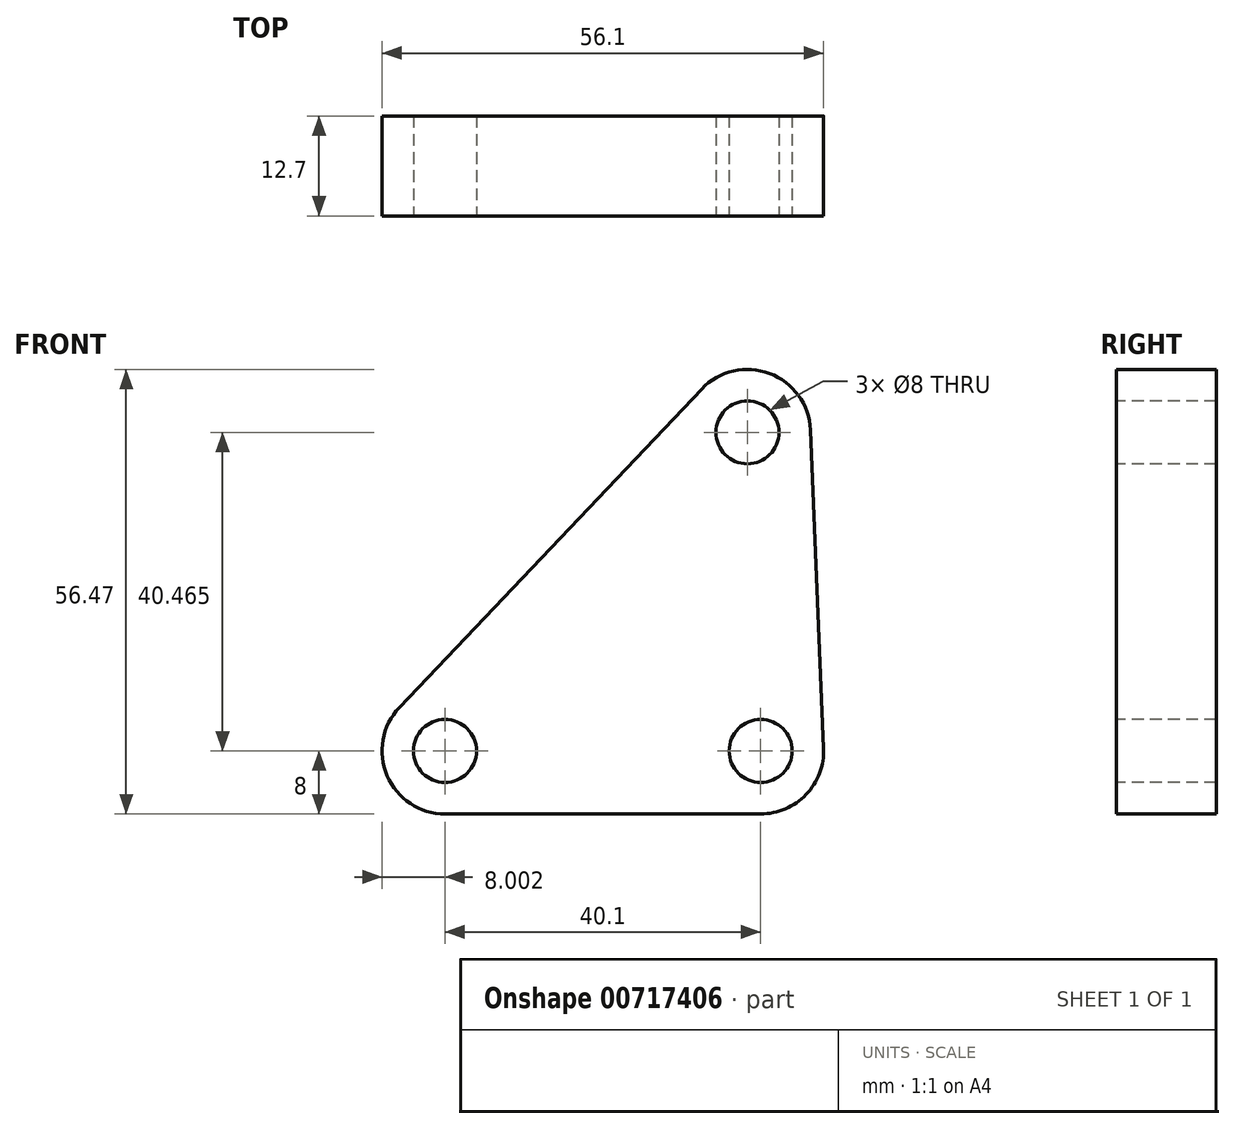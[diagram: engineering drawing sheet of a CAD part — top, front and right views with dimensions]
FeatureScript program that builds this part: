
annotation { "Feature Type Name" : "Feature", "Feature Type Description" : "" }
export const myFeature = defineFeature(function(context is Context, id is Id, definition is map)
    precondition{}
    {
        {
            var Q0;
            Q0=qCreatedBy(makeId("Front.planeOp"),FACE);
            var sketch = newSketch(context, id + "F0", { "sketchPlane" : qUnion([Q0])});
            skLineSegment(sketch, "E0", {"start": v(-13.55, 0) * mm, "end": v(-15.23, 40.47) * mm});
            skLineSegment(sketch, "E1", {"start": v(-15.23, 40.47) * mm, "end": v(-53.65, 0) * mm});
            skLineSegment(sketch, "E2", {"start": v(-53.65, 0) * mm, "end": v(-13.55, 0) * mm});
            skCircle(sketch, "E3", {"center": v(-15.23, 40.47) * mm, "radius": 8 * mm});
            skCircle(sketch, "E4", {"center": v(-13.55, 0) * mm, "radius": 8 * mm});
            skCircle(sketch, "E5", {"center": v(-53.65, 0) * mm, "radius": 8 * mm});
            skLineSegment(sketch, "E6", {"start": v(-59.45, 5.5) * mm, "end": v(-21.03, 45.97) * mm});
            skLineSegment(sketch, "E7", {"start": v(-7.23, 40.8) * mm, "end": v(-5.55, 0.33) * mm});
            skLineSegment(sketch, "E8", {"start": v(-53.65, -8) * mm, "end": v(-13.55, -8) * mm});
            skSolve(sketch);
        }
        {
            var Q0;
            {var subQ2=sQuery(id+"F0.wireOp",EDGE,"E0");var subQ4=sQuery(id+"F0.wireOp",EDGE,"E2");var subQ5=makeQuery(id+"F0.imprint","INTERSECT",VERTEX,{"derivedFrom":[subQ2,subQ4]});Q0=makeQuery(id+"F0.imprint","IMPRINT",FACE,{"disambiguationData":[TD([[makeQuery(id+"F0.imprint","IMPRINT",EDGE,{"disambiguationData":[TD([[subQ5,-1.0]])],"derivedFrom":subQ2}),-1.0]])]});}
            var Q1;
            {var subQ5=sQuery(id+"F0.wireOp",EDGE,"E7");Q1=makeQuery(id+"F0.imprint","IMPRINT",FACE,{"disambiguationData":[TD([[makeQuery(id+"F0.imprint","IMPRINT",EDGE,{"derivedFrom":subQ5}),-1.0]])]});}
            var Q2;
            {var subQ2=sQuery(id+"F0.wireOp",EDGE,"E1");var subQ5=sQuery(id+"F0.wireOp",EDGE,"E0");var subQ6=makeQuery(id+"F0.imprint","INTERSECT",VERTEX,{"derivedFrom":[subQ5,subQ2]});Q2=makeQuery(id+"F0.imprint","IMPRINT",FACE,{"disambiguationData":[TD([[makeQuery(id+"F0.imprint","IMPRINT",EDGE,{"disambiguationData":[TD([[subQ6,1.0]])],"derivedFrom":subQ5}),-1.0]])]});}
            var Q3;
            {var subQ5=sQuery(id+"F0.wireOp",EDGE,"E6");Q3=makeQuery(id+"F0.imprint","IMPRINT",FACE,{"disambiguationData":[TD([[makeQuery(id+"F0.imprint","IMPRINT",EDGE,{"derivedFrom":subQ5}),-1.0]])]});}
            var Q4;
            {var subQ3=sQuery(id+"F0.wireOp",EDGE,"E1");var subQ5=sQuery(id+"F0.wireOp",EDGE,"E2");var subQ6=makeQuery(id+"F0.imprint","INTERSECT",VERTEX,{"derivedFrom":[subQ3,subQ5]});Q4=makeQuery(id+"F0.imprint","IMPRINT",FACE,{"disambiguationData":[TD([[makeQuery(id+"F0.imprint","IMPRINT",EDGE,{"disambiguationData":[TD([[subQ6,1.0]])],"derivedFrom":subQ3}),-1.0]])]});}
            var Q5;
            {var subQ5=sQuery(id+"F0.wireOp",EDGE,"E8");Q5=makeQuery(id+"F0.imprint","IMPRINT",FACE,{"disambiguationData":[TD([[makeQuery(id+"F0.imprint","IMPRINT",EDGE,{"derivedFrom":subQ5}),1.0]])]});}
            var Q6;
            {var subQ3=sQuery(id+"F0.wireOp",EDGE,"E4");var subQ9=sQuery(id+"F0.wireOp",EDGE,"E0");var subQ11=makeQuery(id+"F0.imprint","INTERSECT",VERTEX,{"derivedFrom":[subQ9,subQ3]});Q6=makeQuery(id+"F0.imprint","IMPRINT",FACE,{"disambiguationData":[TD([[makeQuery(id+"F0.imprint","IMPRINT",EDGE,{"disambiguationData":[TD([[subQ11,-1.0]])],"derivedFrom":subQ9}),1.0]])]});}
            var Q7;
            {var subQ0=sQuery(id+"F0.wireOp",EDGE,"E1");var subQ1=sQuery(id+"F0.wireOp",EDGE,"E0");var subQ2=makeQuery(id+"F0.imprint","INTERSECT",VERTEX,{"derivedFrom":[subQ1,subQ0]});Q7=makeQuery(id+"F0.imprint","IMPRINT",FACE,{"disambiguationData":[TD([[makeQuery(id+"F0.imprint","IMPRINT",EDGE,{"disambiguationData":[TD([[subQ2,1.0]])],"derivedFrom":subQ1}),1.0]])]});}
            var Q8;
            {var subQ0=sQuery(id+"F0.wireOp",EDGE,"E2");var subQ1=sQuery(id+"F0.wireOp",EDGE,"E0");var subQ2=makeQuery(id+"F0.imprint","INTERSECT",VERTEX,{"derivedFrom":[subQ1,subQ0]});Q8=makeQuery(id+"F0.imprint","IMPRINT",FACE,{"disambiguationData":[TD([[makeQuery(id+"F0.imprint","IMPRINT",EDGE,{"disambiguationData":[TD([[subQ2,-1.0]])],"derivedFrom":subQ1}),1.0]])]});}
            var Q9;
            {var subQ0=sQuery(id+"F0.wireOp",EDGE,"E2");var subQ1=sQuery(id+"F0.wireOp",EDGE,"E1");var subQ2=makeQuery(id+"F0.imprint","INTERSECT",VERTEX,{"derivedFrom":[subQ1,subQ0]});Q9=makeQuery(id+"F0.imprint","IMPRINT",FACE,{"disambiguationData":[TD([[makeQuery(id+"F0.imprint","IMPRINT",EDGE,{"disambiguationData":[TD([[subQ2,1.0]])],"derivedFrom":subQ1}),1.0]])]});}
            extrude(context, id + "F1", {"entities" : qUnion([Q0, Q1, Q2, Q3, Q4, Q5, Q6, Q7, Q8, Q9]), "depth" : 12.7 * mm, "offsetDistance" : 25.4 * mm});
        }
        {
            var Q0;
            Q0=makeQuery(id+"F1.opExtrude","CAP_FACE",FACE,{"disambiguationData":[OSD([sQuery(id+"F0.wireOp",EDGE,"E3"),sQuery(id+"F0.wireOp",EDGE,"E4"),sQuery(id+"F0.wireOp",EDGE,"E5"),sQuery(id+"F0.wireOp",EDGE,"E6"),sQuery(id+"F0.wireOp",EDGE,"E7"),sQuery(id+"F0.wireOp",EDGE,"E8")])],"isStart":false});
            var sketch = newSketch(context, id + "F2", { "sketchPlane" : qUnion([Q0])});
            skCircle(sketch, "E9", {"center": v(-15.23, 40.47) * mm, "radius": 4 * mm});
            skCircle(sketch, "E10", {"center": v(-13.55, 0) * mm, "radius": 4 * mm});
            skCircle(sketch, "E11", {"center": v(-53.65, 0) * mm, "radius": 4 * mm});
            skSolve(sketch);
        }
        {
            var Q0;
            Q0=makeQuery(id+"F2.imprint","IMPRINT",FACE,{"disambiguationData":[TD([[makeQuery(id+"F2.imprint","IMPRINT",EDGE,{"derivedFrom":sQuery(id+"F2.wireOp",EDGE,"E9")}),1.0]])]});
            var Q1;
            Q1=makeQuery(id+"F2.imprint","IMPRINT",FACE,{"disambiguationData":[TD([[makeQuery(id+"F2.imprint","IMPRINT",EDGE,{"derivedFrom":sQuery(id+"F2.wireOp",EDGE,"E10")}),1.0]])]});
            var Q2;
            Q2=makeQuery(id+"F2.imprint","IMPRINT",FACE,{"disambiguationData":[TD([[makeQuery(id+"F2.imprint","IMPRINT",EDGE,{"derivedFrom":sQuery(id+"F2.wireOp",EDGE,"E11")}),1.0]])]});
            extrude(context, id + "F3", {"entities" : qUnion([Q0, Q1, Q2]), "operationType" : NewBodyOperationType.REMOVE, "endBound" : BoundingType.UP_TO_NEXT, "oppositeDirection" : true, "depth" : 25.4 * mm, "offsetDistance" : 25.4 * mm});
        }
    });
